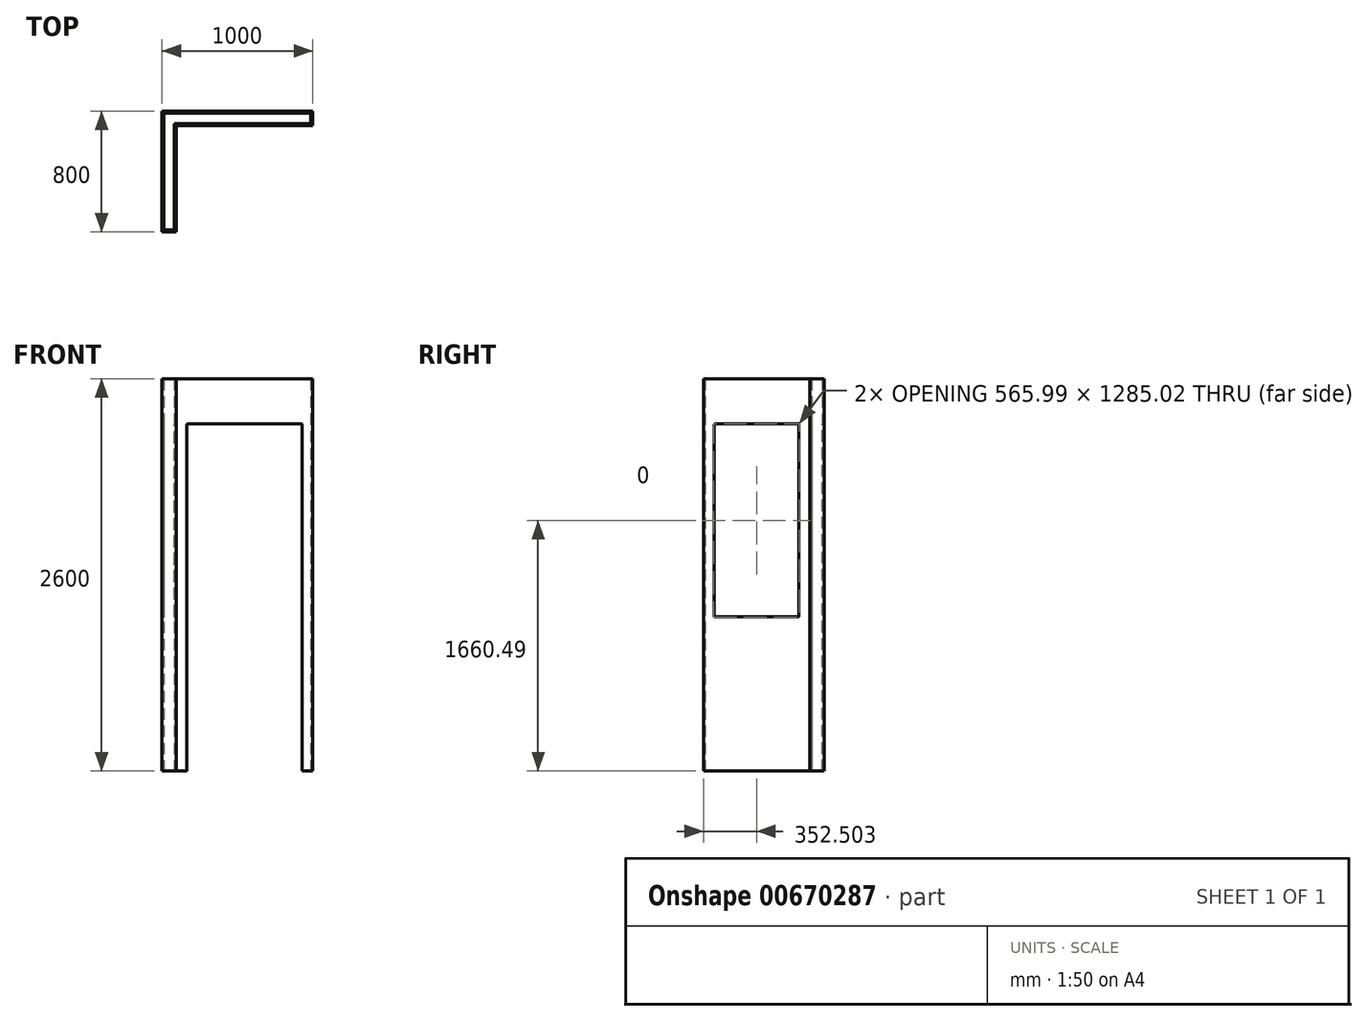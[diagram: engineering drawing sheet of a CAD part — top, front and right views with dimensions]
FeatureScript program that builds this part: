
annotation { "Feature Type Name" : "Feature", "Feature Type Description" : "" }
export const myFeature = defineFeature(function(context is Context, id is Id, definition is map)
    precondition{}
    {
        {
            var Q0;
            Q0=qCreatedBy(makeId("Top.planeOp"),FACE);
            var sketch = newSketch(context, id + "F0", { "sketchPlane" : qUnion([Q0])});
            skLineSegment(sketch, "E0", {"start": v(-271.64, -244.87) * mm, "end": v(-271.64, 555.13) * mm});
            skLineSegment(sketch, "E1", {"start": v(-271.64, 555.13) * mm, "end": v(728.36, 555.13) * mm});
            skLineSegment(sketch, "E2", {"start": v(728.36, 555.13) * mm, "end": v(728.36, 460.13) * mm});
            skLineSegment(sketch, "E3", {"start": v(728.36, 460.13) * mm, "end": v(-176.64, 460.13) * mm});
            skLineSegment(sketch, "E4", {"start": v(-176.64, 460.13) * mm, "end": v(-176.64, -244.87) * mm});
            skLineSegment(sketch, "E5", {"start": v(-176.64, -244.87) * mm, "end": v(-271.64, -244.87) * mm});
            skLineSegment(sketch, "E6.0", {"start": v(715.86, 542.63) * mm, "end": v(715.86, 472.63) * mm});
            skLineSegment(sketch, "E6.1", {"start": v(-189.14, 472.63) * mm, "end": v(-189.14, -232.37) * mm});
            skLineSegment(sketch, "E6.2", {"start": v(-189.14, -232.37) * mm, "end": v(-259.14, -232.37) * mm});
            skLineSegment(sketch, "E6.3", {"start": v(715.86, 472.63) * mm, "end": v(-189.14, 472.63) * mm});
            skLineSegment(sketch, "E6.4", {"start": v(-259.14, -232.37) * mm, "end": v(-259.14, 542.63) * mm});
            skLineSegment(sketch, "E6.5", {"start": v(-259.14, 542.63) * mm, "end": v(715.86, 542.63) * mm});
            skSolve(sketch);
        }
        {
            var Q0;
            Q0=makeQuery(id+"F0.imprint","IMPRINT",FACE,{"disambiguationData":[TD([[makeQuery(id+"F0.imprint","IMPRINT",EDGE,{"derivedFrom":sQuery(id+"F0.wireOp",EDGE,"E0")}),-1.0]])]});
            extrude(context, id + "F1", {"entities" : qUnion([Q0]), "depth" : 2600 * mm, "offsetDistance" : 25 * mm});
        }
        {
            var Q0;
            Q0=makeQuery(id+"F1.opExtrude","SWEPT_FACE",FACE,{"disambiguationData":[OSD([sQuery(id+"F0.wireOp",EDGE,"E4")])]});
            var sketch = newSketch(context, id + "F2", { "sketchPlane" : qUnion([Q0])});
            skLineSegment(sketch, "E7", {"start": v(107.63, 2600) * mm, "end": v(107.63, 1660.49) * mm, "construction": true});
            skLineSegment(sketch, "E8.bottom", {"start": v(387.63, 1020.97) * mm, "end": v(-172.37, 1020.97) * mm});
            skLineSegment(sketch, "E8.top", {"start": v(387.63, 2300) * mm, "end": v(-172.37, 2300) * mm});
            skLineSegment(sketch, "E8.left", {"start": v(387.63, 1020.97) * mm, "end": v(387.63, 2300) * mm});
            skLineSegment(sketch, "E8.right", {"start": v(-172.37, 1020.97) * mm, "end": v(-172.37, 2300) * mm});
            skPoint(sketch, "E8.middle", {"position": v(107.63, 1660.49) * mm});
            skSolve(sketch);
        }
        {
            var Q0;
            Q0=makeQuery(id+"F2.imprint","IMPRINT",FACE,{"disambiguationData":[TD([[makeQuery(id+"F2.imprint","IMPRINT",EDGE,{"derivedFrom":sQuery(id+"F2.wireOp",EDGE,"E8.bottom")}),-1.0]])]});
            extrude(context, id + "F3", {"entities" : qUnion([Q0]), "operationType" : NewBodyOperationType.REMOVE, "endBound" : BoundingType.THROUGH_ALL, "oppositeDirection" : true, "depth" : 95 * mm, "offsetDistance" : 25 * mm});
        }
        {
            var Q0;
            Q0=makeQuery(id+"F1.opExtrude","SWEPT_FACE",FACE,{"disambiguationData":[OSD([sQuery(id+"F0.wireOp",EDGE,"E3")])]});
            var sketch = newSketch(context, id + "F4", { "sketchPlane" : qUnion([Q0])});
            skLineSegment(sketch, "E9.0", {"start": v(658.36, 2300) * mm, "end": v(658.36, 0) * mm});
            skLineSegment(sketch, "E10.0", {"start": v(-106.64, 2300) * mm, "end": v(-106.64, 0) * mm});
            skLineSegment(sketch, "E11.0", {"start": v(658.36, 2300) * mm, "end": v(-106.64, 2300) * mm});
            skSolve(sketch);
        }
        {
            var Q0;
            {var subQ0=sQuery(id+"F4.wireOp",EDGE,"E9.0");Q0=makeQuery(id+"F4.imprint","IMPRINT",FACE,{"disambiguationData":[TD([[makeQuery(id+"F4.imprint","IMPRINT",EDGE,{"derivedFrom":subQ0}),-1.0]])]});}
            extrude(context, id + "F5", {"entities" : qUnion([Q0]), "operationType" : NewBodyOperationType.REMOVE, "endBound" : BoundingType.THROUGH_ALL, "oppositeDirection" : true, "depth" : 25 * mm, "offsetDistance" : 25 * mm});
        }
        {
            var Q0;
            Q0=makeQuery(id+"F5.boolean.opBoolean","COPY",FACE,{"derivedFrom":makeQuery(id+"F5.opExtrude","SWEPT_FACE",FACE,{"disambiguationData":[OSD([sQuery(id+"F4.wireOp",EDGE,"E10.0")])]})});
            var Q1;
            Q1=makeQuery(id+"F5.boolean.opBoolean","COPY",FACE,{"derivedFrom":makeQuery(id+"F5.opExtrude","SWEPT_FACE",FACE,{"disambiguationData":[OSD([sQuery(id+"F4.wireOp",EDGE,"E11.0")])]})});
            var Q2;
            Q2=makeQuery(id+"F3.boolean.opBoolean","COPY",FACE,{"derivedFrom":makeQuery(id+"F3.opExtrude","SWEPT_FACE",FACE,{"disambiguationData":[OSD([sQuery(id+"F2.wireOp",EDGE,"E8.top")])]})});
            var Q3;
            Q3=makeQuery(id+"F3.boolean.opBoolean","COPY",FACE,{"derivedFrom":makeQuery(id+"F3.opExtrude","SWEPT_FACE",FACE,{"disambiguationData":[OSD([sQuery(id+"F2.wireOp",EDGE,"E8.left")])]})});
            fillet(context, id + "F6", {"entities" : qUnion([Q0, Q1, Q2, Q3]), "radius" : 3 * mm, "tangentPropagation" : true, "allowEdgeOverflow" : false});
        }
    });
